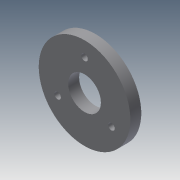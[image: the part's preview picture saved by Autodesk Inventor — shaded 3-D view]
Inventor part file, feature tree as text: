
AUTODESK INVENTOR PART (.ipt)
format: ipt  version: 2013 (Build 170138000, 138)  size: 83,456 bytes
history: native  units: mm
features: extrude x1, sketch x1
ambient origin geometry x8: Origin, YZ Plane, XZ Plane, XY Plane, X Axis, Y Axis, Z Axis, Center Point
bodies: Solid1 (feature_tree)
feature tree (2):
  extrude  "Extrusion1"  [1 undecoded]
  sketch  "Sketch1"  dims[d13=5.0mm d14=0.0mm]
note: 1 required parameter value undecoded (feature->parameter linkage not recoverable at this tier; creation-order binding heuristic only, values carry confidence <= 0.55)
